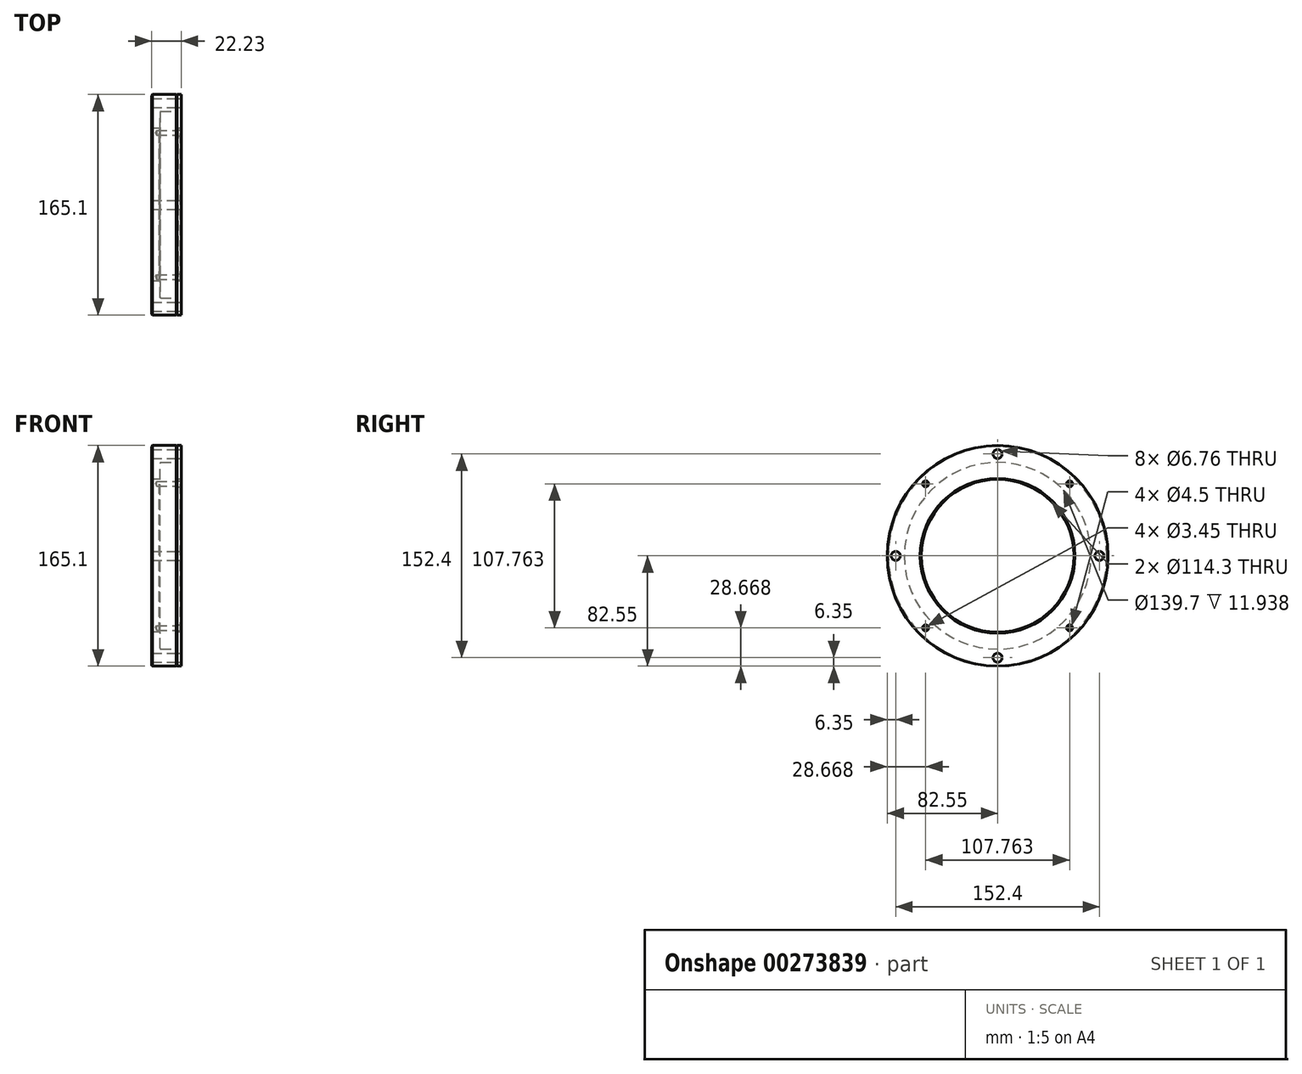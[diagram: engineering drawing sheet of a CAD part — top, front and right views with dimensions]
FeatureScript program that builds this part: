
annotation { "Feature Type Name" : "Feature", "Feature Type Description" : "" }
export const myFeature = defineFeature(function(context is Context, id is Id, definition is map)
    precondition{}
    {
        {
            var Q0;
            Q0=qCreatedBy(makeId("Right.planeOp"),FACE);
            var sketch = newSketch(context, id + "F0", { "sketchPlane" : qUnion([Q0])});
            skCircle(sketch, "E0", {"center": v(0, 0) * mm, "radius": 82.55 * mm});
            skCircle(sketch, "E1", {"center": v(0, 0) * mm, "radius": 57.15 * mm});
            skSolve(sketch);
        }
        {
            var Q0;
            Q0 = qSketchRegion(id + "F0", true);
            extrude(context, id + "F1", {"entities" : qUnion([Q0]), "depth" : 19.05 * mm});
        }
        {
            var Q0;
            Q0=makeQuery(id+"F1.opExtrude","CAP_FACE",FACE,{"disambiguationData":[OSD([sQuery(id+"F0.wireOp",EDGE,"E0"),sQuery(id+"F0.wireOp",EDGE,"E1")])],"isStart":false});
            var sketch = newSketch(context, id + "F2", { "sketchPlane" : qUnion([Q0])});
            skCircle(sketch, "E2", {"center": v(0, 0) * mm, "radius": 69.85 * mm});
            skSolve(sketch);
        }
        {
            var Q0;
            Q0 = qSketchRegion(id + "F2", true);
            extrude(context, id + "F3", {"entities" : qUnion([Q0]), "operationType" : NewBodyOperationType.REMOVE, "oppositeDirection" : true, "depth" : 12.7 * mm});
        }
        {
            var Q0;
            Q0=makeQuery(id+"F1.opExtrude","CAP_FACE",FACE,{"disambiguationData":[OSD([sQuery(id+"F0.wireOp",EDGE,"E0"),sQuery(id+"F0.wireOp",EDGE,"E1")])],"isStart":false});
            var sketch = newSketch(context, id + "F4", { "sketchPlane" : qUnion([Q0])});
            skLineSegment(sketch, "E3", {"start": v(0, 69.85) * mm, "end": v(0, 82.55) * mm, "construction": true});
            skCircle(sketch, "E4.0", {"center": v(0, 0) * mm, "radius": 69.85 * mm, "construction": true});
            skCircle(sketch, "E5.0", {"center": v(0, 0) * mm, "radius": 82.55 * mm, "construction": true});
            skLineSegment(sketch, "E6", {"start": v(0, 76.2) * mm, "end": v(4.42, 76.2) * mm, "construction": true});
            skCircle(sketch, "E7", {"center": v(0, 0) * mm, "radius": 76.2 * mm, "construction": true});
            skPoint(sketch, "E8", {"position": v(0, 76.2) * mm});
            skPoint(sketch, "E9.1.0", {"position": v(-76.2, 0) * mm});
            skPoint(sketch, "E9.2.0", {"position": v(0, -76.2) * mm});
            skPoint(sketch, "E9.3.0", {"position": v(76.2, 0) * mm});
            skSolve(sketch);
        }
        {
            var Q0;
            Q0=sQuery(id+"F4.wireOp",VERTEX,"E8");
            var Q1;
            Q1=sQuery(id+"F4.wireOp",VERTEX,"E9.3.0");
            var Q2;
            Q2=sQuery(id+"F4.wireOp",VERTEX,"E9.2.0");
            var Q3;
            Q3=sQuery(id+"F4.wireOp",VERTEX,"E9.1.0");
            var Q4;
            Q4=makeQuery(id+"F1.opExtrude","SWEPT_BODY",BODY,{"disambiguationData":[OSD([sQuery(id+"F0.wireOp",EDGE,"E0"),sQuery(id+"F0.wireOp",EDGE,"E1")])]});
            hole(context, id + "F5", {"style" : HoleStyle.SIMPLE, "endStyle" : HoleEndStyle.THROUGH, "standardTappedOrClearance" : lookupTablePath({ "standard" : "ANSI", "fit" : "Normal (ASME)", "size" : "1/4", "type" : "Clearance" }), "standardBlindInLast" : lookupTablePath({ "fit" : "Free", "standard" : "ANSI", "size" : "1/4", "type" : "Clearance" }), "holeDiameter" : 6.76 * mm, "tappedDepth" : 12.7 * mm, "tapClearance" : 3, "startFromSketch" : true, "locations" : qUnion([Q0, Q1, Q2, Q3]), "scope" : qUnion([Q4])});
        }
        {
            var Q0;
            Q0=makeQuery(id+"F1.opExtrude","CAP_FACE",FACE,{"disambiguationData":[OSD([sQuery(id+"F0.wireOp",EDGE,"E0"),sQuery(id+"F0.wireOp",EDGE,"E1")])],"isStart":false});
            var sketch = newSketch(context, id + "F6", { "sketchPlane" : qUnion([Q0])});
            skCircle(sketch, "E10.0", {"center": v(0, 0) * mm, "radius": 76.2 * mm, "construction": true});
            skLineSegment(sketch, "E11", {"start": v(0, 0) * mm, "end": v(0, 109.97) * mm, "construction": true});
            skLineSegment(sketch, "E12", {"start": v(0, 0) * mm, "end": v(-85.33, 85.33) * mm, "construction": true});
            skPoint(sketch, "E13", {"position": v(-53.88, 53.88) * mm});
            skPoint(sketch, "E14.1.0", {"position": v(-53.88, -53.88) * mm});
            skPoint(sketch, "E14.2.0", {"position": v(53.88, -53.88) * mm});
            skPoint(sketch, "E14.3.0", {"position": v(53.88, 53.88) * mm});
            skSolve(sketch);
        }
        {
            var Q0;
            Q0=sQuery(id+"F6.wireOp",VERTEX,"E13");
            var Q1;
            Q1=sQuery(id+"F6.wireOp",VERTEX,"E14.3.0");
            var Q2;
            Q2=sQuery(id+"F6.wireOp",VERTEX,"E14.1.0");
            var Q3;
            Q3=sQuery(id+"F6.wireOp",VERTEX,"E14.2.0");
            var Q4;
            Q4=makeQuery(id+"F1.opExtrude","SWEPT_BODY",BODY,{"disambiguationData":[OSD([sQuery(id+"F0.wireOp",EDGE,"E0"),sQuery(id+"F0.wireOp",EDGE,"E1")])]});
            hole(context, id + "F7", {"style" : HoleStyle.SIMPLE, "endStyle" : HoleEndStyle.BLIND, "standardTappedOrClearance" : lookupTablePath({ "standard" : "ANSI", "engagement" : "75%", "pitch" : "32 tpi", "size" : "#8", "type" : "Tapped" }), "standardBlindInLast" : lookupTablePath({ "standard" : "ANSI", "engagement" : "75%", "pitch" : "32 tpi", "size" : "#8", "type" : "Tapped" }), "holeDiameter" : 3.45 * mm, "showTappedDepth" : true, "holeDepth" : 15.08 * mm, "tappedDepth" : 12.7 * mm, "tapClearance" : 3, "startFromSketch" : true, "locations" : qUnion([Q0, Q1, Q2, Q3]), "scope" : qUnion([Q4]), "majorDiameter" : 4.17 * mm});
        }
        {
            var Q0;
            Q0=makeQuery(id+"F3.boolean.opBoolean","COPY",EDGE,{"derivedFrom":makeQuery(id+"F3.opExtrude","CAP_EDGE",EDGE,{"disambiguationData":[OSD([sQuery(id+"F2.wireOp",EDGE,"E2")])],"isStart":true})});
            var Q1;
            Q1=makeQuery(id+"F1.opExtrude","CAP_EDGE",EDGE,{"disambiguationData":[OSD([sQuery(id+"F0.wireOp",EDGE,"E0")])],"isStart":false});
            var Q2;
            Q2=makeQuery(id+"F1.opExtrude","CAP_EDGE",EDGE,{"disambiguationData":[OSD([sQuery(id+"F0.wireOp",EDGE,"E0")])],"isStart":true});
            var Q3;
            Q3=makeQuery(id+"F3.boolean.opBoolean","INTERSECT",EDGE,{"derivedFrom":[makeQuery(id+"F1.opExtrude","SWEPT_FACE",FACE,{"disambiguationData":[OSD([sQuery(id+"F0.wireOp",EDGE,"E1")])]}),makeQuery(id+"F3.opExtrude","CAP_FACE",FACE,{"disambiguationData":[OSD([sQuery(id+"F2.wireOp",EDGE,"E2")])],"isStart":false})]});
            var Q4;
            Q4=makeQuery(id+"F1.opExtrude","CAP_EDGE",EDGE,{"disambiguationData":[OSD([sQuery(id+"F0.wireOp",EDGE,"E1")])],"isStart":true});
            chamfer(context, id + "F8", {"entities" : qUnion([Q0, Q1, Q2, Q3, Q4]), "width" : 0.76 * mm, "tangentPropagation" : true});
        }
        {
            var Q0;
            Q0=makeQuery(id+"F3.boolean.opBoolean","COPY",EDGE,{"derivedFrom":makeQuery(id+"F3.opExtrude","CAP_EDGE",EDGE,{"disambiguationData":[OSD([sQuery(id+"F2.wireOp",EDGE,"E2")])],"isStart":false})});
            fillet(context, id + "F9", {"entities" : qUnion([Q0]), "radius" : 0.76 * mm, "tangentPropagation" : true, "allowEdgeOverflow" : false});
        }
        {
            var Q0;
            Q0=makeQuery(id+"F4.imprint","IMPRINT",FACE,{"disambiguationData":[TD([[makeQuery(id+"F4.imprint","IMPRINT",EDGE,{"derivedFrom":makeQuery(id+"F1.opExtrude","CAP_EDGE",EDGE,{"disambiguationData":[OSD([sQuery(id+"F0.wireOp",EDGE,"E0")])],"isStart":false})}),1.0]])]});
            var sketch = newSketch(context, id + "F10", { "sketchPlane" : qUnion([Q0])});
            skCircle(sketch, "E15.0", {"center": v(0, 0) * mm, "radius": 57.15 * mm});
            skCircle(sketch, "E16.0", {"center": v(0, 0) * mm, "radius": 82.55 * mm});
            skCircle(sketch, "E17.0", {"center": v(-53.88, 53.88) * mm, "radius": 1.73 * mm, "construction": true});
            skCircle(sketch, "E18.0", {"center": v(53.88, 53.88) * mm, "radius": 1.73 * mm, "construction": true});
            skCircle(sketch, "E19.0", {"center": v(53.88, -53.88) * mm, "radius": 1.73 * mm, "construction": true});
            skCircle(sketch, "E20.0", {"center": v(-53.88, -53.88) * mm, "radius": 1.73 * mm, "construction": true});
            skSolve(sketch);
        }
        {
            var Q0;
            Q0=makeQuery(id+"F4.imprint","IMPRINT",FACE,{"disambiguationData":[TD([[makeQuery(id+"F4.imprint","IMPRINT",EDGE,{"derivedFrom":makeQuery(id+"F1.opExtrude","CAP_EDGE",EDGE,{"disambiguationData":[OSD([sQuery(id+"F0.wireOp",EDGE,"E0")])],"isStart":false})}),1.0]])]});
            var Q1;
            Q1=makeQuery(id+"F10.imprint","IMPRINT",FACE,{"disambiguationData":[TD([[makeQuery(id+"F10.imprint","IMPRINT",EDGE,{"derivedFrom":sQuery(id+"F10.wireOp",EDGE,"E15.0")}),-1.0]])]});
            extrude(context, id + "F11", {"entities" : qUnion([Q0, Q1]), "depth" : 3.17 * mm});
        }
        {
            var Q0;
            Q0=makeQuery(id+"F11.opExtrude","SWEPT_BODY",BODY,{"disambiguationData":[OSD([sQuery(id+"F2.wireOp",EDGE,"E2"),sQuery(id+"F10.wireOp",EDGE,"E15.0")])]});
            var Q1;
            Q1=makeQuery(id+"F11.opExtrude","SWEPT_BODY",BODY,{"disambiguationData":[OSD([sQuery(id+"F0.wireOp",EDGE,"E0"),sQuery(id+"F2.wireOp",EDGE,"E2")])]});
            booleanBodies(context, id + "F12", {"operationType" : BooleanOperationType.UNION, "tools" : qUnion([Q0, Q1])});
        }
        {
            var Q0;
            {var subQ0=sQuery(id+"F2.wireOp",EDGE,"E2");Q0=makeQuery(id+"F12.opBoolean","MERGE",FACE,{"derivedFrom":[makeQuery(id+"F11.opExtrude","CAP_FACE",FACE,{"disambiguationData":[OSD([sQuery(id+"F0.wireOp",EDGE,"E0"),subQ0])],"isStart":false}),makeQuery(id+"F11.opExtrude","CAP_FACE",FACE,{"disambiguationData":[OSD([subQ0,sQuery(id+"F10.wireOp",EDGE,"E15.0")])],"isStart":false})]});}
            var sketch = newSketch(context, id + "F13", { "sketchPlane" : qUnion([Q0])});
            skCircle(sketch, "E21.0", {"center": v(53.88, 53.88) * mm, "radius": 1.73 * mm, "construction": true});
            skCircle(sketch, "E22.0", {"center": v(-53.88, 53.88) * mm, "radius": 1.73 * mm, "construction": true});
            skCircle(sketch, "E23.0", {"center": v(53.88, -53.88) * mm, "radius": 1.73 * mm, "construction": true});
            skCircle(sketch, "E24.0", {"center": v(-53.88, -53.88) * mm, "radius": 1.73 * mm, "construction": true});
            skSolve(sketch);
        }
        {
            var Q0;
            Q0=sQuery(id+"F13.wireOp",VERTEX,"E22.0.center");
            var Q1;
            Q1=sQuery(id+"F13.wireOp",VERTEX,"E21.0.center");
            var Q2;
            Q2=sQuery(id+"F13.wireOp",VERTEX,"E24.0.center");
            var Q3;
            Q3=sQuery(id+"F13.wireOp",VERTEX,"E23.0.center");
            var Q4;
            Q4=makeQuery(id+"F11.opExtrude","SWEPT_BODY",BODY,{"disambiguationData":[OSD([sQuery(id+"F2.wireOp",EDGE,"E2"),sQuery(id+"F10.wireOp",EDGE,"E15.0")])]});
            hole(context, id + "F14", {"style" : HoleStyle.SIMPLE, "endStyle" : HoleEndStyle.THROUGH, "standardTappedOrClearance" : lookupTablePath({ "standard" : "ANSI", "fit" : "Normal (ASME)", "size" : "#8", "type" : "Clearance" }), "standardBlindInLast" : lookupTablePath({ "fit" : "Free", "standard" : "ANSI", "size" : "#8", "type" : "Clearance" }), "holeDiameter" : 4.5 * mm, "tappedDepth" : 12.7 * mm, "tapClearance" : 3, "startFromSketch" : true, "locations" : qUnion([Q0, Q1, Q2, Q3]), "scope" : qUnion([Q4])});
        }
        {
            var Q0;
            Q0=makeQuery(id+"F11.opExtrude","CAP_EDGE",EDGE,{"disambiguationData":[OSD([sQuery(id+"F10.wireOp",EDGE,"E15.0")])],"isStart":false});
            var Q1;
            Q1=makeQuery(id+"F11.opExtrude","CAP_EDGE",EDGE,{"disambiguationData":[OSD([sQuery(id+"F10.wireOp",EDGE,"E15.0")])],"isStart":true});
            chamfer(context, id + "F15", {"entities" : qUnion([Q0, Q1]), "width" : 0.76 * mm, "tangentPropagation" : true});
        }
        {
            var Q0;
            {var subQ0=sQuery(id+"F2.wireOp",EDGE,"E2");Q0=makeQuery(id+"F12.opBoolean","MERGE",FACE,{"derivedFrom":[makeQuery(id+"F11.opExtrude","CAP_FACE",FACE,{"disambiguationData":[OSD([sQuery(id+"F0.wireOp",EDGE,"E0"),subQ0])],"isStart":false}),makeQuery(id+"F11.opExtrude","CAP_FACE",FACE,{"disambiguationData":[OSD([subQ0,sQuery(id+"F10.wireOp",EDGE,"E15.0")])],"isStart":false})]});}
            var sketch = newSketch(context, id + "F16", { "sketchPlane" : qUnion([Q0])});
            skCircle(sketch, "E25.0", {"center": v(0, 76.2) * mm, "radius": 3.38 * mm, "construction": true});
            skCircle(sketch, "E26.0", {"center": v(76.2, 0) * mm, "radius": 3.38 * mm, "construction": true});
            skCircle(sketch, "E27.0", {"center": v(0, -76.2) * mm, "radius": 3.38 * mm, "construction": true});
            skCircle(sketch, "E28.0", {"center": v(-76.2, 0) * mm, "radius": 3.38 * mm, "construction": true});
            skSolve(sketch);
        }
        {
            var Q0;
            Q0=sQuery(id+"F16.wireOp",VERTEX,"E25.0.center");
            var Q1;
            Q1=sQuery(id+"F16.wireOp",VERTEX,"E28.0.center");
            var Q2;
            Q2=sQuery(id+"F16.wireOp",VERTEX,"E27.0.center");
            var Q3;
            Q3=sQuery(id+"F16.wireOp",VERTEX,"E26.0.center");
            var Q4;
            Q4=makeQuery(id+"F11.opExtrude","SWEPT_BODY",BODY,{"disambiguationData":[OSD([sQuery(id+"F2.wireOp",EDGE,"E2"),sQuery(id+"F10.wireOp",EDGE,"E15.0")])]});
            hole(context, id + "F17", {"style" : HoleStyle.SIMPLE, "endStyle" : HoleEndStyle.THROUGH, "standardTappedOrClearance" : lookupTablePath({ "standard" : "ANSI", "fit" : "Normal (ASME)", "size" : "1/4", "type" : "Clearance" }), "standardBlindInLast" : lookupTablePath({ "fit" : "Free", "standard" : "ANSI", "size" : "1/4", "type" : "Clearance" }), "holeDiameter" : 6.76 * mm, "tappedDepth" : 12.7 * mm, "tapClearance" : 3, "startFromSketch" : true, "locations" : qUnion([Q0, Q1, Q2, Q3]), "scope" : qUnion([Q4])});
        }
    });
